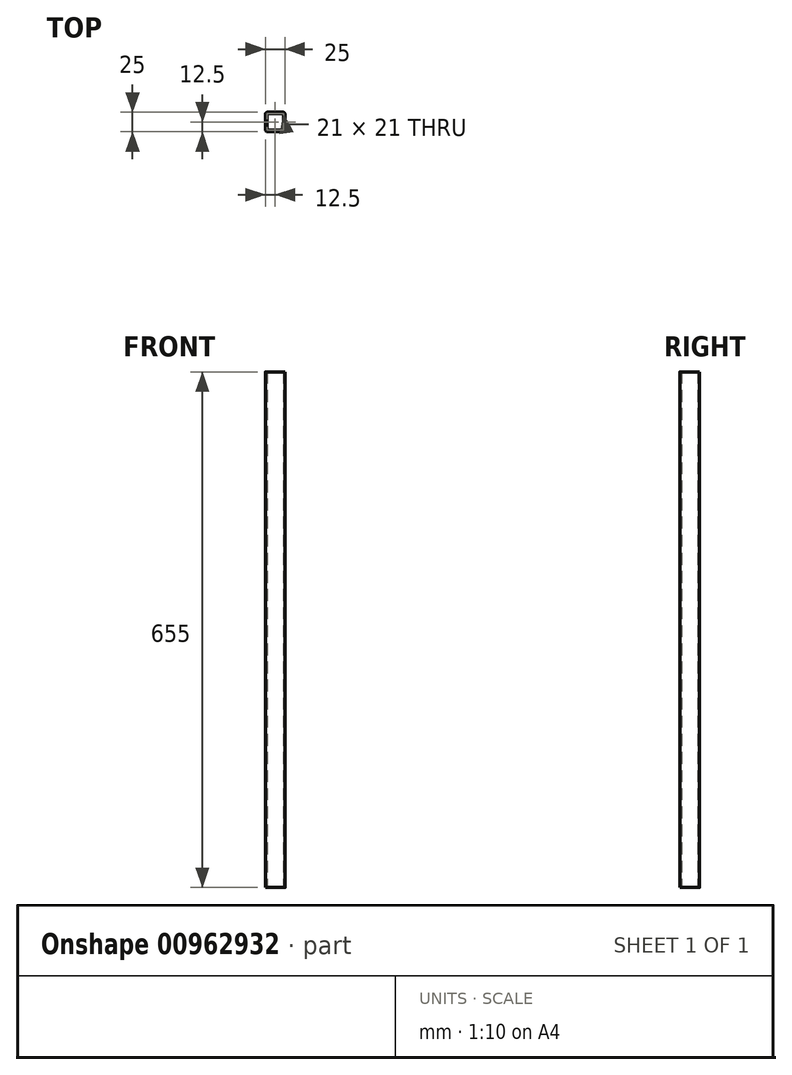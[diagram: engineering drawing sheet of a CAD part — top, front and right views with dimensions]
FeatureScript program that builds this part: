
annotation { "Feature Type Name" : "Feature", "Feature Type Description" : "" }
export const myFeature = defineFeature(function(context is Context, id is Id, definition is map)
    precondition{}
    {
        {
            var Q0;
            Q0=qCreatedBy(makeId("Top.planeOp"),FACE);
            var sketch = newSketch(context, id + "F0", { "sketchPlane" : qUnion([Q0])});
            skLineSegment(sketch, "E0.bottom", {"start": v(9.5, 12.5) * mm, "end": v(-9.5, 12.5) * mm});
            skLineSegment(sketch, "E0.top", {"start": v(9.5, -12.5) * mm, "end": v(-9.5, -12.5) * mm});
            skLineSegment(sketch, "E0.left", {"start": v(12.5, 9.5) * mm, "end": v(12.5, -9.5) * mm});
            skLineSegment(sketch, "E0.right", {"start": v(-12.5, 9.5) * mm, "end": v(-12.5, -9.5) * mm});
            skPoint(sketch, "E0.middle", {"position": v(0, 0) * mm});
            skPoint(sketch, "E1.visualSharp", {"position": v(-12.5, 12.5) * mm});
            skArc(sketch, "E1.filletArc", {"start": v(-9.5, 12.5) * mm, "mid": v(-11.62, 11.62) * mm, "end": v(-12.5, 9.5) * mm});
            skPoint(sketch, "E2.visualSharp", {"position": v(-12.5, -12.5) * mm});
            skArc(sketch, "E2.filletArc", {"start": v(-12.5, -9.5) * mm, "mid": v(-11.62, -11.62) * mm, "end": v(-9.5, -12.5) * mm});
            skPoint(sketch, "E3.visualSharp", {"position": v(12.5, -12.5) * mm});
            skArc(sketch, "E3.filletArc", {"start": v(9.5, -12.5) * mm, "mid": v(11.62, -11.62) * mm, "end": v(12.5, -9.5) * mm});
            skPoint(sketch, "E4.visualSharp", {"position": v(12.5, 12.5) * mm});
            skArc(sketch, "E4.filletArc", {"start": v(12.5, 9.5) * mm, "mid": v(11.62, 11.62) * mm, "end": v(9.5, 12.5) * mm});
            skLineSegment(sketch, "E5.0", {"start": v(10.5, 10.5) * mm, "end": v(-10.5, 10.5) * mm});
            skLineSegment(sketch, "E5.1", {"start": v(10.5, 10.5) * mm, "end": v(10.5, -10.5) * mm});
            skLineSegment(sketch, "E5.2", {"start": v(10.5, -10.5) * mm, "end": v(-10.5, -10.5) * mm});
            skLineSegment(sketch, "E5.3", {"start": v(-10.5, 10.5) * mm, "end": v(-10.5, -10.5) * mm});
            skSolve(sketch);
        }
        {
            var Q0;
            Q0=makeQuery(id+"F0.imprint","IMPRINT",FACE,{"disambiguationData":[TD([[makeQuery(id+"F0.imprint","IMPRINT",EDGE,{"derivedFrom":sQuery(id+"F0.wireOp",EDGE,"E0.bottom")}),1.0]])]});
            extrude(context, id + "F1", {"entities" : qUnion([Q0]), "depth" : 655 * mm, "offsetDistance" : 25 * mm});
        }
    });
